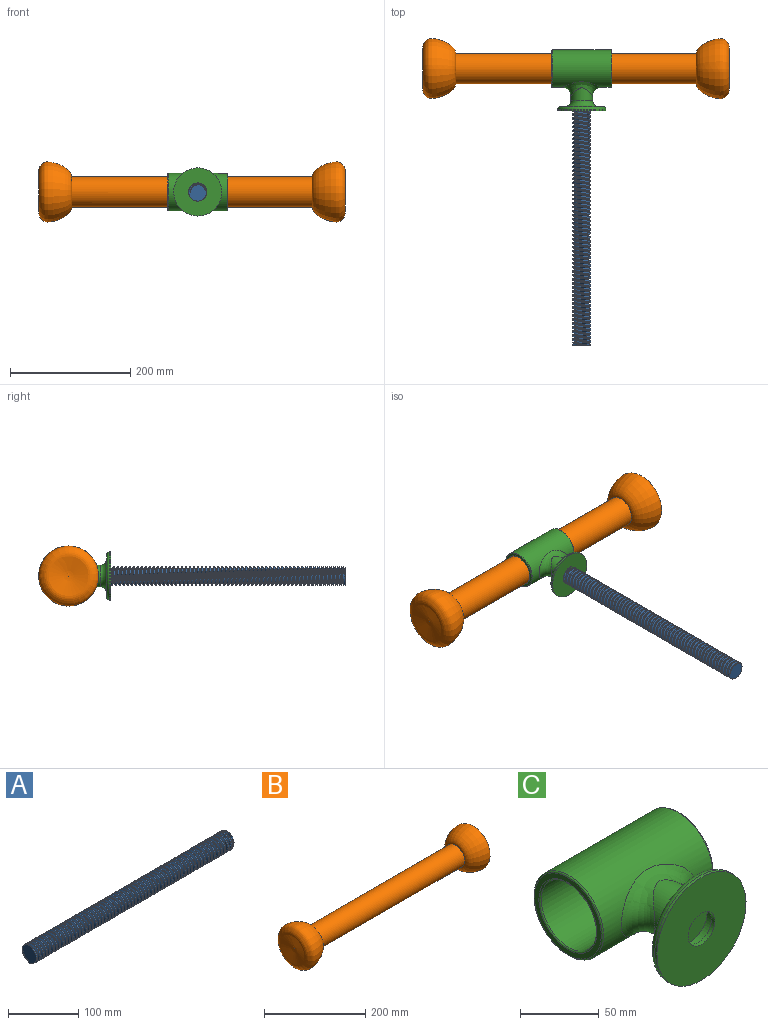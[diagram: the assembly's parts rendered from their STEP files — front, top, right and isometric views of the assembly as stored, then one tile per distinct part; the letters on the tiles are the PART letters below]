
ASSEMBLY  parts=3 mates=2
PART A: 8 faces, bbox 405.8x36x31.3 mm
  f0: plane 31.31x30.46mm, normal (-1,0,0), area 653.6mm2, adj f1,f3,f4,f5
  f1: cylinder r=15mm len=400mm, axis (1,0,0), area 12085.7mm2, adj f0,f2,f3,f4,f6,f7
  f2: plane 31.32x30.47mm, normal (1,0,0), area 653.6mm2, adj f1,f5,f6,f7
  f3: plane 3x2.23mm, normal (0,1,0), area 4.1mm2, adj f0,f1,f5,f7
  f4: bspline ~401.73x34.64mm, area 17672.1mm2, adj f0,f1,f5,f6
  f5: cylinder r=12mm len=400mm, axis (-1,0,0), area 5787mm2, adj f0,f2,f3,f4,f6,f7
  f6: plane 3x2.23mm, normal (0,-1,0), area 4.1mm2, adj f1,f2,f4,f5
  f7: bspline ~401.73x34.64mm, area 17603.8mm2, adj f1,f2,f3,f5
PART B: 3 faces, bbox 509.9x100x100 mm
  f0: cylinder r=25mm len=400mm, axis (-1,0,0), area 62831.9mm2, adj f1,f2
  f1: revolved ~99.98x99.98mm, area 23655.9mm2, adj f0
  f2: revolved ~99.98x99.98mm, area 23655.9mm2, adj f0
PART C: 25 faces, bbox 100x105.1x86.6 mm
  f0: cylinder r=18mm len=36mm, axis (0,-1,0), area 1545.5mm2, adj f1,f14
  f1: torus R=28mm, axis (0,-1,0), area 2135.2mm2, adj f0,f2
  f2: plane 70x70mm, normal (0,1,0), area 1385.4mm2, adj f1,f3
  f3: torus R=35mm, axis (0,-1,0), area 1884.3mm2, adj f2,f4
  f4: cylinder r=40mm len=80mm, axis (0,-1,0), area 502.7mm2, adj f3,f5
  f5: plane 80x80mm, normal (0,-1,0), area 4574.2mm2, adj f4,f6
  f6: cylinder r=12mm len=24mm, axis (0,-1,0), area 226.2mm2, adj f5,f7
  f7: plane 30x30mm, normal (0,1,0), area 254.5mm2, adj f6,f8
  f8: cylinder r=15mm len=30mm, axis (0,-1,0), area 659.7mm2, adj f7,f9
  f9: plane 30x30mm, normal (0,-1,0), area 706.9mm2, adj f8
  f10: plane 60x60mm, normal (-1,0,0), area 703.7mm2, adj f15,f16
  f11: plane 60x60mm, normal (1,0,0), area 703.7mm2, adj f17,f18
  f12: cylinder r=31mm len=98mm, axis (-1,0,0), area 16591.9mm2, adj f14,f16,f18
  f13: cylinder r=25mm len=98mm, axis (-1,0,0), area 15393.8mm2, adj f15,f17
  f14: bspline ~66.01x44.49mm, area 2438.6mm2, adj f0,f12
  f15: torus R=26mm, axis (1,0,0), area 250.3mm2, adj f10,f13
  f16: torus R=30mm, axis (1,0,0), area 302.4mm2, adj f10,f12
  f17: torus R=26mm, axis (1,0,0), area 250.3mm2, adj f11,f13
  f18: torus R=30mm, axis (1,0,0), area 302.4mm2, adj f11,f12
  f19: cylinder r=15mm len=25.61mm, axis (0,-1,0), area 53.3mm2, adj f20,f21
  f20: plane 25.61x7.19mm, normal (0,1,0), area 130.2mm2, adj f19,f21
  f21: cylinder r=31mm len=25.61mm, axis (-1,0,0), area 139.2mm2, adj f19,f20
  f22: cylinder r=15mm len=25.61mm, axis (0,-1,0), area 53.3mm2, adj f23,f24
  f23: plane 25.61x7.19mm, normal (0,1,0), area 130.2mm2, adj f22,f24
  f24: cylinder r=31mm len=25.61mm, axis (-1,0,0), area 139.2mm2, adj f22,f23
PLACE A rot(axis=(-0.58,0.58,-0.58),120deg) t=(-0.73,0,0.67)mm
PLACE B rot(axis=(0,1,0),0deg) t=(-10.35,460,0.67)mm
PLACE C rot(axis=(0,1,0),0deg) t=(-0.73,390,0.67)mm
MATE fastened C.f0 <-> A.f1  axis (0,-1,0) through (-0.73,400,0.67)mm
MATE slider C.f12 <-> B.f0  axis (-1,0,0) through (48.27,460,0.67)mm
